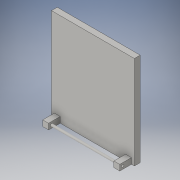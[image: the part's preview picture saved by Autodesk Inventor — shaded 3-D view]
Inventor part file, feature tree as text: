
AUTODESK INVENTOR PART (.ipt)
format: ipt  version: 2016 (Build 200138000, 138)  size: 126,464 bytes
history: native  units: in
note: dims shown in document units (in); Inventor stores cm internally (conversion verified against a paired STEP export)
features: sketch x6, extrude x5, hole x2
ambient origin geometry x8: Origin, YZ Plane, XZ Plane, XY Plane, X Axis, Y Axis, Z Axis, Center Point
bodies: Solid1 (feature_tree)
feature tree (13):
  extrude  "Extrusion1"  Depth=2.0in
  extrude  "Extrusion2"  Depth=0.125in
  extrude  "Extrusion3"  Depth=0.125in
  hole  "Hole1"  [1 undecoded]
  hole  "Hole2"  [1 undecoded]
  extrude  "Extrusion4"  Depth=0.063in
  sketch  "Sketch5"  dims[d10=0.063in d11=0.063in d12=0.05in d13=0.75in d14=0.375in d15=0.25in d16=0.5635in d17=1.0in d18=0.8108in]
  extrude  "Extrusion5"  Depth=1.404in TaperAngle=0.0deg
  sketch  "Sketch1"  dims[d0=1.78in d1=2.0in]
  sketch  "Sketch2"  dims[d2=0.125in d3=0.0in d4=0.125in]
  sketch  "Sketch3"  dims[d5=0.25in d6=0.0in d7=0.125in]
  sketch  "Sketch4"  dims[d8=0.25in d9=0.0in]
  sketch  "Sketch6"  dims[d19=0.063in d33=1.0in d21=0.05in d22=0.75in d23=0.375in d24=0.25in d25=0.5635in d26=1.0in d27=0.8108in d28=1.404in d29=0.0in d30=0.063in d31=0.063in d32=1.404in d34=0.0in]
note: 2 required parameter values undecoded (feature->parameter linkage not recoverable at this tier; creation-order binding heuristic only, values carry confidence <= 0.55)
